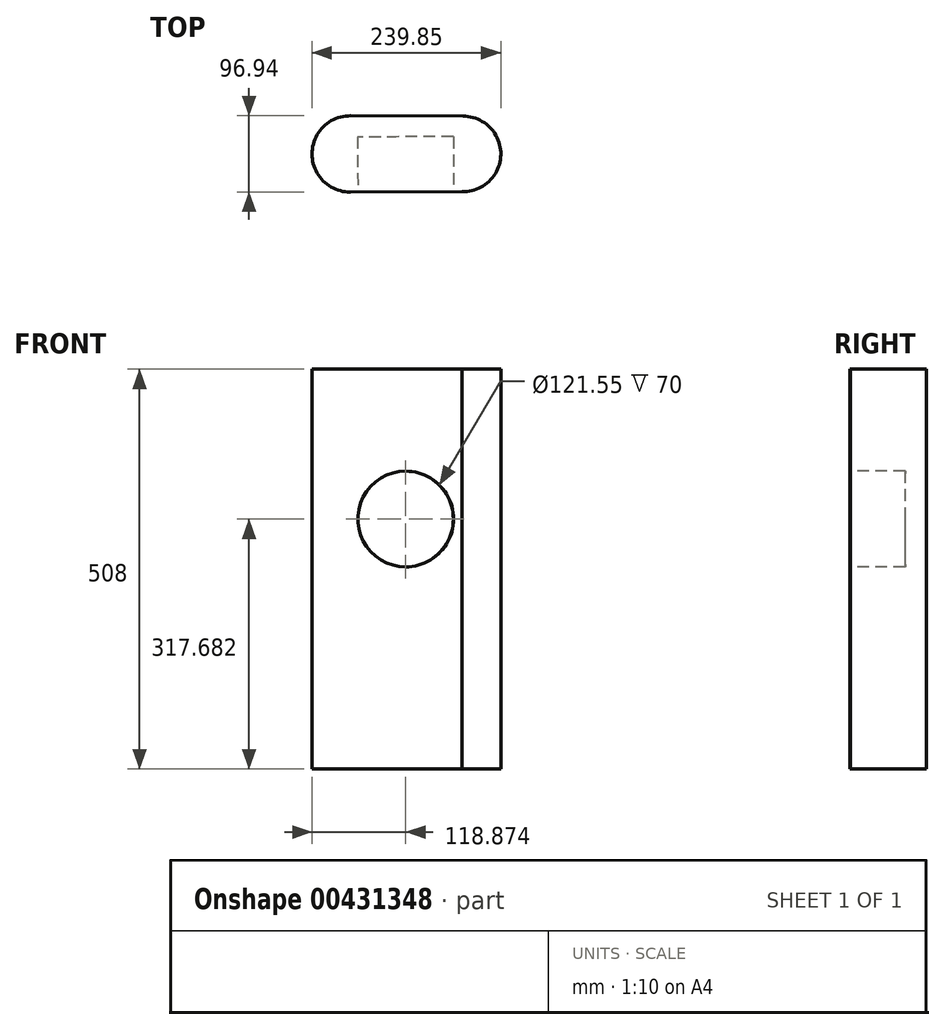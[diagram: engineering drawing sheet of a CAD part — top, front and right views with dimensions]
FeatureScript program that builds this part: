
annotation { "Feature Type Name" : "Feature", "Feature Type Description" : "" }
export const myFeature = defineFeature(function(context is Context, id is Id, definition is map)
    precondition{}
    {
        {
            var Q0;
            Q0=qCreatedBy(makeId("Top.planeOp"),FACE);
            var sketch = newSketch(context, id + "F0", { "sketchPlane" : qUnion([Q0])});
            skArc(sketch, "E0", {"start": v(0.32, 48.46) * mm, "mid": v(-48.47, 0.07) * mm, "end": v(0.17, -48.47) * mm});
            skArc(sketch, "E1", {"start": v(141.77, -47.97) * mm, "mid": v(191.37, -0.89) * mm, "end": v(143.54, 48) * mm});
            skLineSegment(sketch, "E2", {"start": v(0, 48.47) * mm, "end": v(143.54, 48) * mm});
            skLineSegment(sketch, "E3", {"start": v(145.33, -47.96) * mm, "end": v(0.17, -48.47) * mm});
            skSolve(sketch);
        }
        {
            var Q0;
            Q0 = qSketchRegion(id + "F0", true);
            extrude(context, id + "F1", {"entities" : qUnion([Q0]), "oppositeDirection" : true, "depth" : 508 * mm});
        }
        {
            var Q0;
            Q0=makeQuery(id+"F1.opExtrude","SWEPT_FACE",FACE,{"disambiguationData":[OSD([sQuery(id+"F0.wireOp",EDGE,"E3")])]});
            var sketch = newSketch(context, id + "F2", { "sketchPlane" : qUnion([Q0])});
            skCircle(sketch, "E4", {"center": v(70.36, -190.32) * mm, "radius": 60.77 * mm});
            skSolve(sketch);
        }
        {
            var Q0;
            Q0 = qSketchRegion(id + "F2", true);
            extrude(context, id + "F3", {"entities" : qUnion([Q0]), "operationType" : NewBodyOperationType.REMOVE, "oppositeDirection" : true, "depth" : 70 * mm});
        }
    });
